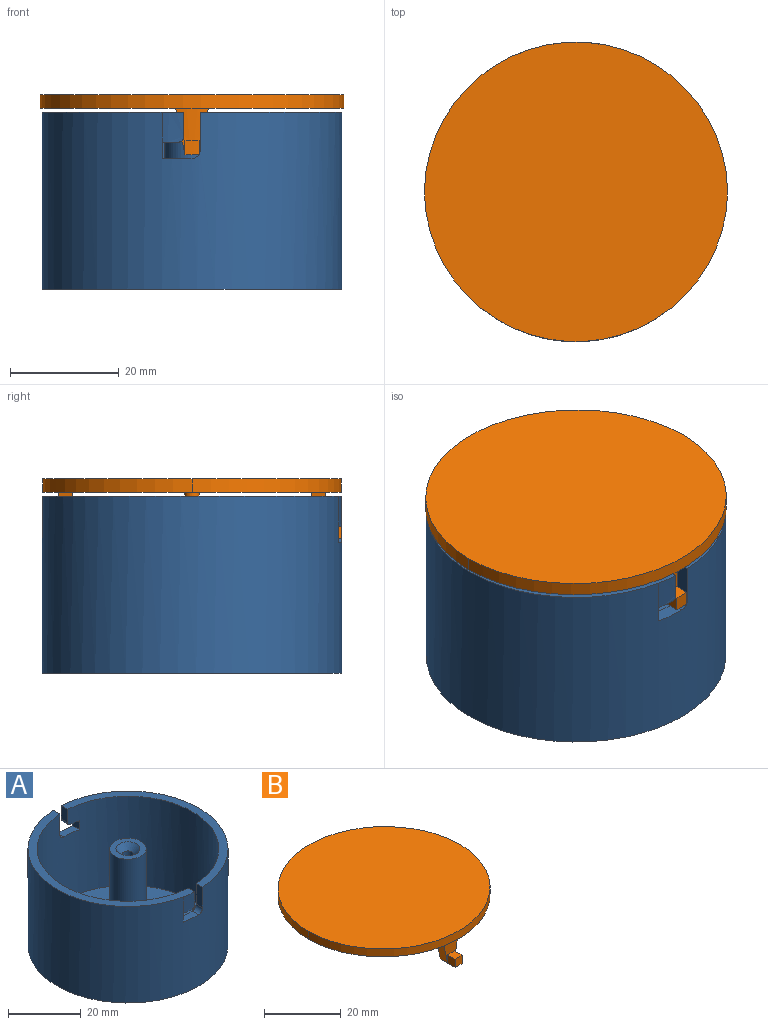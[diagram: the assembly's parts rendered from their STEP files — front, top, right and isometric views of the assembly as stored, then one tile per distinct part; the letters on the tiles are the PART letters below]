
ASSEMBLY  parts=2 mates=1
PART A: 27 faces, bbox 55x55x32.5 mm
  f0: plane 3x3mm, normal (0,0,1), area 7.1mm2, adj f16
  f1: cylinder r=25mm len=50mm, axis (0,0,-1), area 4615.6mm2, adj f2,f5,f6,f9,f10,f11,f12,f14
  f2: cylinder r=25mm len=5.5mm, axis (0,0,-1), area 22mm2, adj f1,f6,f7,f8,f13
  f3: cylinder r=27.5mm len=55mm, axis (0,0,-1), area 5518.9mm2, adj f4,f5,f6,f9,f10,f11,f12,f15
  f4: cylinder r=27.5mm len=5.5mm, axis (0,0,-1), area 22mm2, adj f3,f6,f7,f8,f13
  f5: plane 54.92x26mm, normal (0,0,1), area 198.7mm2, adj f1,f3,f12,f26
  f6: plane 54.92x26mm, normal (0,0,1), area 198.7mm2, adj f1,f2,f3,f4,f13,f25
  f7: cylinder r=1mm len=2.58mm, axis (0,-1,0), area 3.9mm2, adj f2,f4,f8,f13
  f8: plane 3x3mm, normal (0,0,-1), area 7.6mm2, adj f2,f4,f7,f9
  f9: plane 3x2.56mm, normal (1,0,0), area 7.7mm2, adj f1,f3,f8,f10
  f10: plane 5.5x3.11mm, normal (0,0,1), area 13.9mm2, adj f1,f3,f9,f11
  f11: cylinder r=1.5mm len=2.55mm, axis (0,-1,0), area 5.9mm2, adj f1,f3,f10,f12
  f12: plane 7x2.5mm, normal (-1,0,0), area 17.5mm2, adj f1,f3,f5,f11
  f13: plane 4.5x2.5mm, normal (1,0,0), area 11.3mm2, adj f2,f4,f6,f7
  f14: plane 50x50mm, normal (0,0,1), area 1885mm2, adj f1,f17
  f15: plane 55x55mm, normal (0,0,-1), area 2375.8mm2, adj f3
  f16: cylinder r=1.5mm len=28.2mm, axis (0,0,-1), area 265.8mm2, adj f0,f19
  f17: cylinder r=5mm len=30mm, axis (0,0,-1), area 942.5mm2, adj f14,f18
  f18: plane 10x10mm, normal (0,0,1), area 44.3mm2, adj f17,f19
  f19: cone r=1.5mm half-angle=45deg, axis (0,0,1), area 38.4mm2, adj f16,f18
  f20: cylinder r=1mm len=2.58mm, axis (0,1,0), area 3.9mm2, adj f1,f3,f21,f26
  f21: plane 3x3mm, normal (0,0,-1), area 7.6mm2, adj f1,f3,f20,f22
  f22: plane 3x2.56mm, normal (-1,0,0), area 7.7mm2, adj f1,f3,f21,f23
  f23: plane 5.5x3.11mm, normal (0,0,1), area 13.9mm2, adj f1,f3,f22,f24
  f24: cylinder r=1.5mm len=2.55mm, axis (0,1,0), area 5.9mm2, adj f1,f3,f23,f25
  f25: plane 7x2.5mm, normal (1,0,0), area 17.5mm2, adj f1,f3,f6,f24
  f26: plane 4.5x2.5mm, normal (-1,0,0), area 11.3mm2, adj f1,f3,f5,f20
PART B: 24 faces, bbox 55.7x55x11.5 mm
  f0: cylinder r=24.7mm len=8.5mm, axis (0,0,1), area 29.9mm2, adj f4,f5,f6,f8,f9,f21
  f1: cylinder r=27.85mm len=55.7mm, axis (0,0,-1), area 217mm2, adj f21,f22,f23
  f2: cylinder r=24.7mm len=8.5mm, axis (0,0,1), area 29.9mm2, adj f12,f13,f14,f16,f17,f21
  f3: plane 5.5x2.6mm, normal (0,0,-1), area 14.3mm2, adj f5,f6,f7,f8,f9,f10
  f4: plane 2.83x2.6mm, normal (0,0,1), area 7.3mm2, adj f0,f5,f6,f10
  f5: plane 2.8x2.6mm, normal (-1,0,0), area 7.3mm2, adj f0,f3,f4,f10
  f6: plane 2.8x2.6mm, normal (1,0,0), area 7.3mm2, adj f0,f3,f4,f10
  f7: plane 8.5x6mm, normal (0,-1,0), area 36.6mm2, adj f3,f8,f9,f21
  f8: plane 8.51x2.68mm, normal (0.98,0,-0.2), area 22.5mm2, adj f0,f3,f7,f21
  f9: plane 8.51x2.68mm, normal (-0.98,0,-0.2), area 22.5mm2, adj f0,f3,f7,f21
  f10: cylinder r=27.85mm len=2.6mm, axis (0,0,1), area 6.8mm2, adj f3,f4,f5,f6
  f11: plane 5.5x2.6mm, normal (0,0,-1), area 14.3mm2, adj f13,f14,f15,f16,f17,f18
  f12: plane 2.83x2.6mm, normal (0,0,1), area 7.3mm2, adj f2,f13,f14,f18
  f13: plane 2.8x2.6mm, normal (1,0,0), area 7.3mm2, adj f2,f11,f12,f18
  f14: plane 2.8x2.6mm, normal (-1,0,0), area 7.3mm2, adj f2,f11,f12,f18
  f15: plane 8.5x6mm, normal (0,1,0), area 36.6mm2, adj f11,f16,f17,f21
  f16: plane 8.51x2.68mm, normal (-0.98,0,-0.2), area 22.5mm2, adj f2,f11,f15,f21
  f17: plane 8.51x2.68mm, normal (0.98,0,-0.2), area 22.5mm2, adj f2,f11,f15,f21
  f18: cylinder r=27.85mm len=2.6mm, axis (0,0,1), area 6.8mm2, adj f11,f12,f13,f14
  f19: cone r=1.4mm half-angle=3deg, axis (0,0,1), area 65.9mm2, adj f20,f21
  f20: plane 1.86x1.86mm, normal (0,0,-1), area 2.7mm2, adj f19
  f21: plane 55.7x55mm, normal (0,0,-1), area 2360.1mm2, adj f0,f1,f2,f7,f8,f9,f15,f16
  f22: cylinder r=27.85mm len=55.7mm, axis (0,0,-1), area 217mm2, adj f1,f21,f23
  f23: plane 55.7x55mm, normal (0,0,1), area 2397.9mm2, adj f1,f22
PLACE A at identity
PLACE B t=(0,0,30.7)mm
MATE revolute B.f19 <-> A.f16  axis (0,0,-1) through (0,0,30.7)mm
